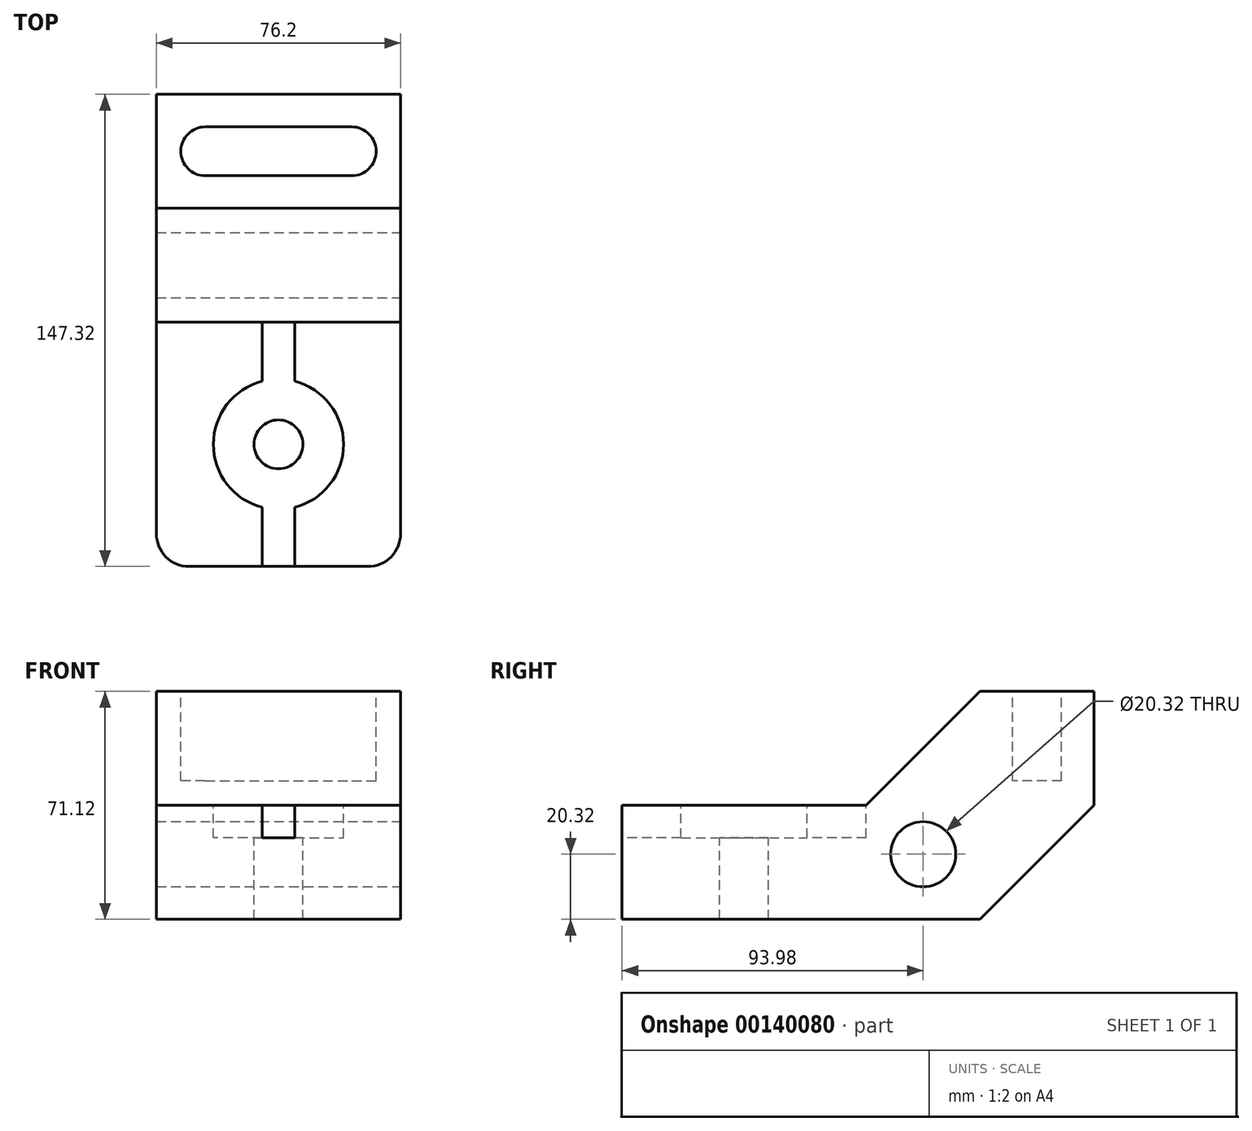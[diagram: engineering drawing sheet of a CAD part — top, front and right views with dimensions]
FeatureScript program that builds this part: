
annotation { "Feature Type Name" : "Feature", "Feature Type Description" : "" }
export const myFeature = defineFeature(function(context is Context, id is Id, definition is map)
    precondition{}
    {
        {
            var Q0;
            Q0=qCreatedBy(makeId("Right.planeOp"),FACE);
            var sketch = newSketch(context, id + "F0", { "sketchPlane" : qUnion([Q0])});
            skLineSegment(sketch, "E0", {"start": v(0, 0) * mm, "end": v(111.76, 0) * mm});
            skLineSegment(sketch, "E1", {"start": v(111.76, 0) * mm, "end": v(147.32, 35.56) * mm});
            skLineSegment(sketch, "E2", {"start": v(147.32, 35.56) * mm, "end": v(147.32, 71.12) * mm});
            skLineSegment(sketch, "E3", {"start": v(147.32, 71.12) * mm, "end": v(111.76, 71.12) * mm});
            skLineSegment(sketch, "E4", {"start": v(111.76, 71.12) * mm, "end": v(76.2, 35.56) * mm});
            skLineSegment(sketch, "E5", {"start": v(76.2, 35.56) * mm, "end": v(0, 35.56) * mm});
            skLineSegment(sketch, "E6", {"start": v(0, 35.56) * mm, "end": v(0, 0) * mm});
            skSolve(sketch);
        }
        {
            var Q0;
            Q0 = qSketchRegion(id + "F0", true);
            extrude(context, id + "F1", {"entities" : qUnion([Q0]), "depth" : 76.2 * mm});
        }
        {
            var Q0;
            Q0=makeQuery(id+"F1.opExtrude","CAP_FACE",FACE,{"disambiguationData":[OSD([sQuery(id+"F0.wireOp",EDGE,"E0"),sQuery(id+"F0.wireOp",EDGE,"E1"),sQuery(id+"F0.wireOp",EDGE,"E2"),sQuery(id+"F0.wireOp",EDGE,"E3"),sQuery(id+"F0.wireOp",EDGE,"E4"),sQuery(id+"F0.wireOp",EDGE,"E5"),sQuery(id+"F0.wireOp",EDGE,"E6")])],"isStart":false});
            var sketch = newSketch(context, id + "F2", { "sketchPlane" : qUnion([Q0])});
            skLineSegment(sketch, "E7", {"start": v(-60.19, 20.32) * mm, "end": v(203.93, 20.32) * mm, "construction": true});
            skCircle(sketch, "E8", {"center": v(93.98, 20.32) * mm, "radius": 10.16 * mm});
            skSolve(sketch);
        }
        {
            var Q0;
            Q0 = qSketchRegion(id + "F2", true);
            extrude(context, id + "F3", {"entities" : qUnion([Q0]), "operationType" : NewBodyOperationType.REMOVE, "endBound" : BoundingType.THROUGH_ALL, "oppositeDirection" : true, "depth" : 25.4 * mm});
        }
        {
            var Q0;
            Q0=makeQuery(id+"F1.opExtrude","CAP_EDGE",EDGE,{"disambiguationData":[OSD([sQuery(id+"F0.wireOp",EDGE,"E6")])],"isStart":false});
            var Q1;
            Q1=makeQuery(id+"F1.opExtrude","CAP_EDGE",EDGE,{"disambiguationData":[OSD([sQuery(id+"F0.wireOp",EDGE,"E6")])],"isStart":true});
            fillet(context, id + "F4", {"entities" : qUnion([Q0, Q1]), "radius" : 10.16 * mm, "tangentPropagation" : true, "allowEdgeOverflow" : false});
        }
        {
            var Q0;
            Q0=makeQuery(id+"F1.opExtrude","SWEPT_FACE",FACE,{"disambiguationData":[OSD([sQuery(id+"F0.wireOp",EDGE,"E3")])]});
            var sketch = newSketch(context, id + "F5", { "sketchPlane" : qUnion([Q0])});
            skLineSegment(sketch, "E9", {"start": v(15.24, 137.16) * mm, "end": v(60.96, 137.16) * mm});
            skLineSegment(sketch, "E10", {"start": v(15.24, 121.92) * mm, "end": v(60.96, 121.92) * mm});
            skArc(sketch, "E11", {"start": v(15.24, 137.16) * mm, "mid": v(7.62, 129.54) * mm, "end": v(15.24, 121.92) * mm});
            skArc(sketch, "E12", {"start": v(60.96, 121.92) * mm, "mid": v(68.58, 129.54) * mm, "end": v(60.96, 137.16) * mm});
            skSolve(sketch);
        }
        {
            var Q0;
            Q0=makeQuery(id+"F5.imprint","IMPRINT",FACE,{"disambiguationData":[TD([[makeQuery(id+"F5.imprint","IMPRINT",EDGE,{"derivedFrom":sQuery(id+"F5.wireOp",EDGE,"E9")}),-1.0]])]});
            extrude(context, id + "F6", {"entities" : qUnion([Q0]), "operationType" : NewBodyOperationType.REMOVE, "oppositeDirection" : true, "depth" : 27.94 * mm});
        }
        {
            var Q0;
            Q0=makeQuery(id+"F1.opExtrude","SWEPT_FACE",FACE,{"disambiguationData":[OSD([sQuery(id+"F0.wireOp",EDGE,"E5")])]});
            var sketch = newSketch(context, id + "F7", { "sketchPlane" : qUnion([Q0])});
            skLineSegment(sketch, "E13.bottom", {"start": v(33.02, 76.2) * mm, "end": v(43.18, 76.2) * mm});
            skLineSegment(sketch, "E13.top", {"start": v(33.02, 0) * mm, "end": v(43.18, 0) * mm});
            skLineSegment(sketch, "E13.left", {"start": v(33.02, 76.2) * mm, "end": v(33.02, 0) * mm});
            skLineSegment(sketch, "E13.right", {"start": v(43.18, 76.2) * mm, "end": v(43.18, 0) * mm});
            skLineSegment(sketch, "E14", {"start": v(38.1, 76.2) * mm, "end": v(38.1, 0) * mm, "construction": true});
            skSolve(sketch);
        }
        {
            var Q0;
            Q0=makeQuery(id+"F7.imprint","IMPRINT",FACE,{"disambiguationData":[TD([[makeQuery(id+"F7.imprint","IMPRINT",EDGE,{"derivedFrom":sQuery(id+"F7.wireOp",EDGE,"E13.bottom")}),1.0]])]});
            var sketch = newSketch(context, id + "F8", { "sketchPlane" : qUnion([Q0])});
            skLineSegment(sketch, "E15.0", {"start": v(38.1, 76.2) * mm, "end": v(38.1, 0) * mm});
            skPoint(sketch, "E16", {"position": v(38.1, 38.1) * mm});
            skSolve(sketch);
        }
        {
            var Q0;
            Q0=sQuery(id+"F8.wireOp",VERTEX,"E16");
            var Q1;
            Q1=makeQuery(id+"F1.opExtrude","SWEPT_BODY",BODY,{"disambiguationData":[OSD([sQuery(id+"F0.wireOp",EDGE,"E0"),sQuery(id+"F0.wireOp",EDGE,"E1"),sQuery(id+"F0.wireOp",EDGE,"E2"),sQuery(id+"F0.wireOp",EDGE,"E3"),sQuery(id+"F0.wireOp",EDGE,"E4"),sQuery(id+"F0.wireOp",EDGE,"E5"),sQuery(id+"F0.wireOp",EDGE,"E6")])]});
            hole(context, id + "F9", {"style" : HoleStyle.C_BORE, "endStyle" : HoleEndStyle.THROUGH, "holeDiameter" : 15.24 * mm, "cBoreDiameter" : 40.64 * mm, "cBoreDepth" : 10.16 * mm, "locations" : qUnion([Q0]), "scope" : qUnion([Q1]), "isTappedThrough" : true});
        }
        {
            var Q0;
            Q0 = qSketchRegion(id + "F7", true);
            extrude(context, id + "F10", {"entities" : qUnion([Q0]), "operationType" : NewBodyOperationType.REMOVE, "oppositeDirection" : true, "depth" : 10.16 * mm});
        }
    });
